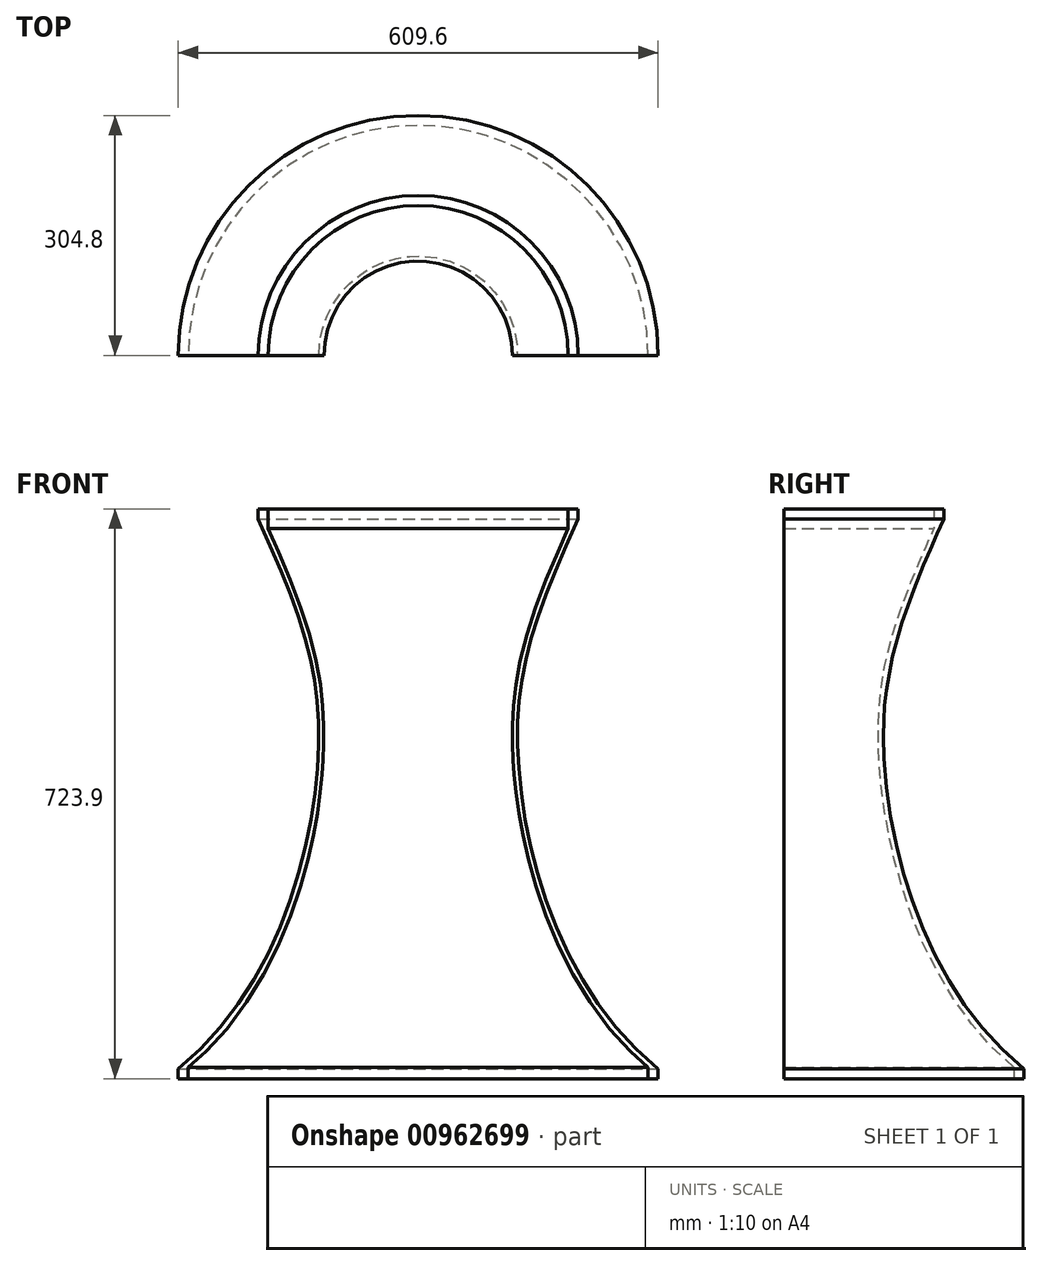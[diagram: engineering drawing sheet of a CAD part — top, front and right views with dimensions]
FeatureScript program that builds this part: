
annotation { "Feature Type Name" : "Feature", "Feature Type Description" : "" }
export const myFeature = defineFeature(function(context is Context, id is Id, definition is map)
    precondition{}
    {
        {
            var Q0;
            Q0=qCreatedBy(makeId("Front.planeOp"),FACE);
            var sketch = newSketch(context, id + "F0", { "sketchPlane" : qUnion([Q0])});
            skLineSegment(sketch, "E0", {"start": v(304.8, 78.92) * mm, "end": v(304.8, 91.62) * mm});
            skLineSegment(sketch, "E1", {"start": v(203.2, 802.82) * mm, "end": v(203.2, 790.12) * mm});
            skFitSpline(sketch, "E2", {"points": [v(203.2, 790.12) * mm, v(127, 485.32) * mm, v(304.8, 91.62) * mm], "startDerivative": vector(-373.26, -821.63) * mm, "endDerivative": vector(678.51, -544.08) * mm});
            skFitSpline(sketch, "E3.0", {"points": [v(197.42, 792.74) * mm, v(189.63, 775.6) * mm, v(175.24, 743.26) * mm, v(157.18, 699.27) * mm, v(142.64, 658.47) * mm, v(131.59, 619.54) * mm, v(125.3, 587.57) * mm, v(122.02, 561.67) * mm, v(120.44, 541.92) * mm, v(119.72, 521.69) * mm, v(119.84, 504.3) * mm, v(120.37, 490) * mm, v(120.98, 479.04) * mm, v(121.8, 467.87) * mm, v(123.2, 452.7) * mm, v(125.5, 433.25) * mm, v(129.2, 409.3) * mm, v(133.88, 384.87) * mm, v(141.45, 351.84) * mm, v(153.55, 310.03) * mm, v(172.56, 260.14) * mm, v(196.37, 211.63) * mm, v(225.3, 165.63) * mm, v(259.68, 123.26) * mm, v(286.44, 98.2) * mm, v(300.83, 86.66) * mm]});
            skLineSegment(sketch, "E4", {"start": v(203.2, 802.82) * mm, "end": v(190.5, 802.82) * mm});
            skLineSegment(sketch, "E5", {"start": v(190.5, 802.82) * mm, "end": v(190.5, 777.42) * mm});
            skLineSegment(sketch, "E6", {"start": v(304.8, 78.92) * mm, "end": v(292.1, 78.92) * mm});
            skLineSegment(sketch, "E7", {"start": v(292.1, 78.92) * mm, "end": v(292.1, 93.89) * mm});
            skSolve(sketch);
        }
        {
            var Q0;
            Q0=qCreatedBy(makeId("Front.planeOp"),FACE);
            var sketch = newSketch(context, id + "F1", { "sketchPlane" : qUnion([Q0])});
            skLineSegment(sketch, "E8", {"start": v(0, 0) * mm, "end": v(0, 788.46) * mm});
            skSolve(sketch);
        }
        {
            var Q0;
            Q0 = qSketchRegion(id + "F0", true);
            var Q1;
            Q1=sQuery(id+"F1.wireOp",EDGE,"E8");
            revolve(context, id + "F2", {"surfaceOperationType" : NewSurfaceOperationType.NEW, "entities" : qUnion([Q0]), "axis" : qUnion([Q1]), "revolveType" : RevolveType.ONE_DIRECTION, "angle" : 180 * degree});
        }
    });
